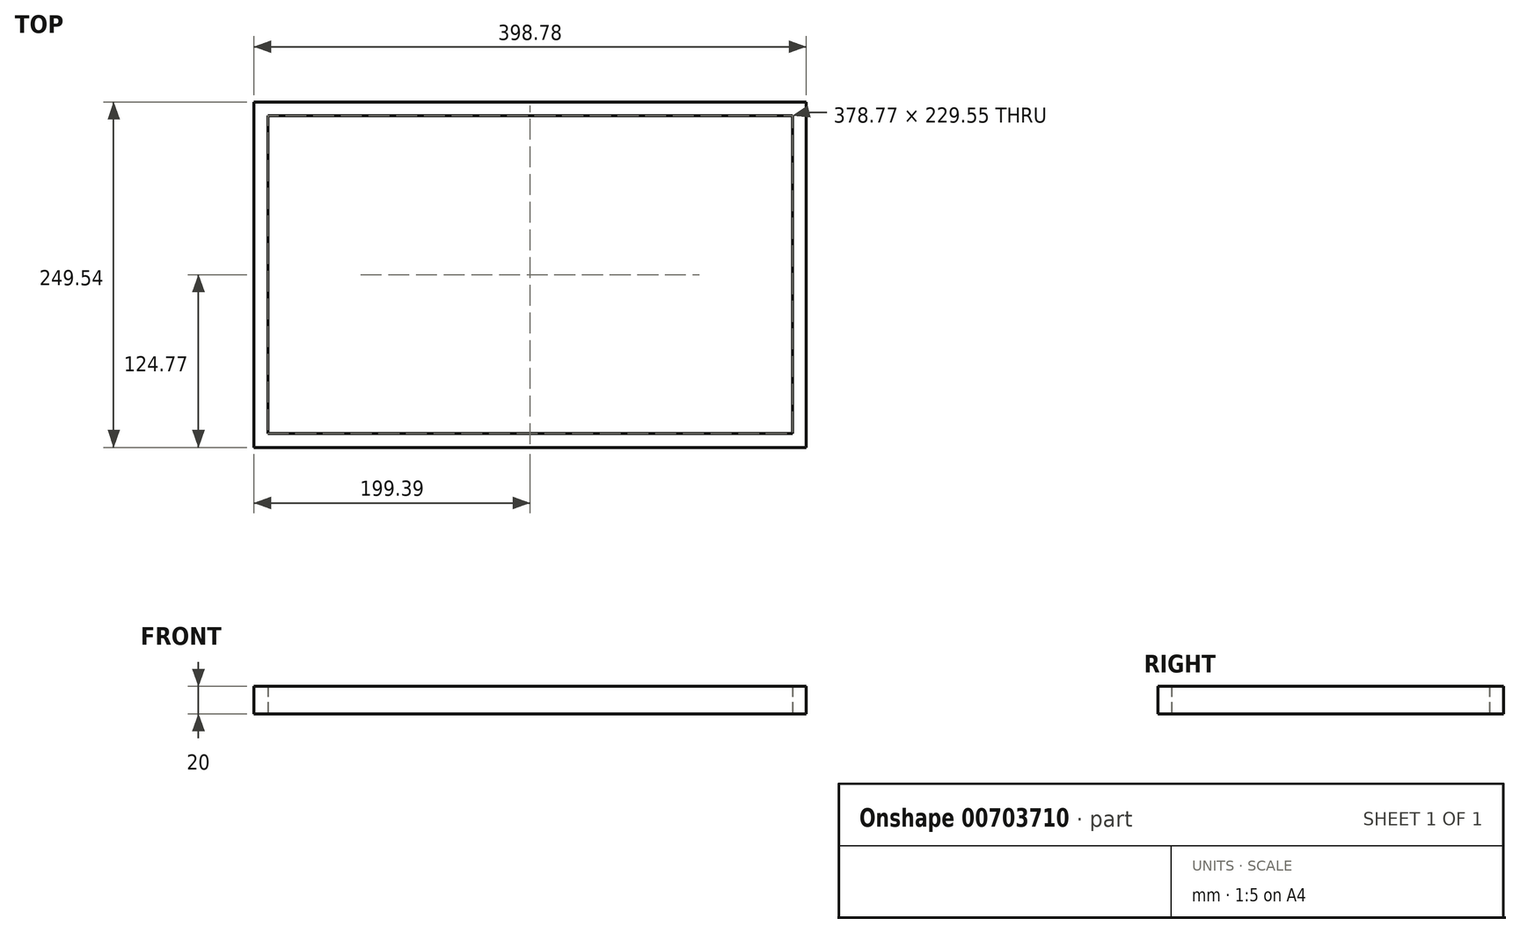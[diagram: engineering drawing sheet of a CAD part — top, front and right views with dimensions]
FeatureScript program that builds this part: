
annotation { "Feature Type Name" : "Feature", "Feature Type Description" : "" }
export const myFeature = defineFeature(function(context is Context, id is Id, definition is map)
    precondition{}
    {
        {
            var Q0;
            Q0=qCreatedBy(makeId("Top.planeOp"),FACE);
            var sketch = newSketch(context, id + "F0", { "sketchPlane" : qUnion([Q0])});
            skLineSegment(sketch, "E0.bottom", {"start": v(179.39, -104.77) * mm, "end": v(-179.39, -104.78) * mm});
            skLineSegment(sketch, "E0.top", {"start": v(179.39, 104.77) * mm, "end": v(-179.39, 104.77) * mm});
            skLineSegment(sketch, "E0.left", {"start": v(179.39, -104.77) * mm, "end": v(179.39, 104.78) * mm});
            skLineSegment(sketch, "E0.right", {"start": v(-179.39, -104.78) * mm, "end": v(-179.39, 104.77) * mm});
            skPoint(sketch, "E0.middle", {"position": v(0, 0) * mm});
            skLineSegment(sketch, "E1.0", {"start": v(173.39, 98.78) * mm, "end": v(-173.39, 98.78) * mm});
            skLineSegment(sketch, "E1.1", {"start": v(173.39, -98.77) * mm, "end": v(173.39, 98.78) * mm});
            skLineSegment(sketch, "E1.2", {"start": v(173.39, -98.77) * mm, "end": v(-173.39, -98.78) * mm});
            skLineSegment(sketch, "E1.3", {"start": v(-173.39, -98.78) * mm, "end": v(-173.39, 98.78) * mm});
            skLineSegment(sketch, "E2.0", {"start": v(189.39, 114.78) * mm, "end": v(-189.39, 114.78) * mm});
            skLineSegment(sketch, "E2.1", {"start": v(189.39, -114.77) * mm, "end": v(189.39, 114.78) * mm});
            skLineSegment(sketch, "E2.2", {"start": v(189.39, -114.77) * mm, "end": v(-189.39, -114.78) * mm});
            skLineSegment(sketch, "E2.3", {"start": v(-189.39, -114.78) * mm, "end": v(-189.39, 114.78) * mm});
            skLineSegment(sketch, "E3.0", {"start": v(199.39, 124.78) * mm, "end": v(-199.39, 124.77) * mm});
            skLineSegment(sketch, "E3.1", {"start": v(199.39, -124.77) * mm, "end": v(199.39, 124.78) * mm});
            skLineSegment(sketch, "E3.2", {"start": v(199.39, -124.77) * mm, "end": v(-199.39, -124.78) * mm});
            skLineSegment(sketch, "E3.3", {"start": v(-199.39, -124.78) * mm, "end": v(-199.39, 124.77) * mm});
            skSolve(sketch);
        }
        {
            var Q0;
            Q0=makeQuery(id+"F0.imprint","IMPRINT",FACE,{"disambiguationData":[TD([[makeQuery(id+"F0.imprint","IMPRINT",EDGE,{"derivedFrom":sQuery(id+"F0.wireOp",EDGE,"E2.0")}),-1.0]])]});
            extrude(context, id + "F1", {"entities" : qUnion([Q0]), "depth" : 20 * mm, "offsetDistance" : 25 * mm});
        }
    });
